# Revit family: Hager-Panelboard Meter Enclosures-Surface_mounted-IP2XC-With_Cover-Hosted-GB-en
name_source: partatom
category: Electrical Equipment
units: mm (PartAtom-declared; Revit-internal decimal feet)

## family parameters
Cut with Voids When Loaded = No
Host = Face
Maintain Annotation Orientation = Yes
Panel Configuration = Two Columns, Circuits Across
Part Type = Panelboard
Room Calculation Point = No
Round Connector Dimension = Use Diameter
Shared = No

## types (8) — shared parameters
BC_MODEL_ID = 1593630
BC_OBJECT_ID = 518755
BC_OBJECT_VERSION = #1
Classification.Uniclass.Pr.Description = Control circuit device enclosures
Classification.Uniclass.Pr.Number = Pr_80_77_28_16
Code hager = ADD-EC000214_UKME
Default Elevation = 1219 mm
EF000003 - Mounting method = Surface mounted
EF000007 - Colour = 0
EF000024 - UV resistant = No
EF000049 - Depth = 160 mm  [stored 0.524934 ft]
EF000116 - RAL-number = 7035
EF000118 - With mounting plate = No
EF001062 - EMC-version = No
EF001088 - Extension possible = No
EF001131 - Internal depth = 400 mm  [stored 1.31234 ft]
EF001134 - DIN-rail = No
EF001596 - Housing material = 0
EF004462 - Type of closure = 0
EF004464 - Type of door = Other
EF005474 - Degree of protection (IP) = IP2XC
EF006244 - Transparent cover/door = No
EF006306 - With lock = No
EF009212 - Cover model = 0
EF015777 - Neutral terminal block = No
EF015941 - Signal passing door = No
ETIM class code = EC000214
ETIM class name = Small distribution board
Ground Bus = No
HG000002-With door or cover = Yes
HG000003-Range = Panelboard Meter Enclosures
HG000005-Thickness = 3 mm  [stored 0.00984252 ft]
HG000006-Flush mounted = No
HG000018 - Cut-outs in left = No
HG000019 - Cut-outs in right = No
HG000019-Cut-outs in right = No
HG000060-RAL-number = 7035
HG000099-Onfly Template ID = 1539920
Manufacturer = Hager
Name = Panelboard Meter Enclosures-Surface_mounted-IP2XC-With_Cover-GB
Name BIM&CO = Electricity
Name hager = ADD_Enclosures_EC000214
Neutral Bus = No
Type Comments = Panelboard Meter Enclosures
Uniformat = Low Tension Service & Dist.
Uniformat code = D501001
zero-valued in all types: EF000218 - Built-in depth, EF000332 - Built-in height, EF000846 - Built-in width, EF001131 - Inner depth

## per-type parameters (varying)
| type | BC_VARIANT_ID | EF000008 - Width | EF000040 - Height | EF000266 - Number of rows | EF000339 - Type of covering | EF002950 - Width in number of modular spacings | EF015776 - Earthing terminal block | HG000001-Number of columns | HG000004-Manufacturer reference | HG000018-Cut-outs in left | HG000025-Number of cut-outs | Model |
| Panelboard Meter Enclosures-Surface_mounted_W350_H1250_D160_4_Modular_Spacing-JF12504SM | 1197421 | 350 mm  [stored 1.14829 ft] | 1250 mm  [stored 4.10105 ft] | 0 | 0 | 4 | No | 1 | JF12504SM | Yes | 4 | JF12504SM |
| Panelboard Meter Enclosures-Surface_mounted_W350_H1400_D160_6_Modular_Spacing-JF14006SM | 1197422 | 350 mm  [stored 1.14829 ft] | 1400 mm  [stored 4.59318 ft] | 0 | 0 | 6 | Yes | 1 | JF14006SM | Yes | 6 | JF14006SM |
| Panelboard Meter Enclosures-Surface_mounted_W350_H1550_D160_8_Modular_Spacing-JF15508SM | 1197423 | 350 mm  [stored 1.14829 ft] | 1550 mm  [stored 5.0853 ft] | 0 | 0 | 8 | No | 1 | JF15508SM | Yes | 8 | JF15508SM |
| Panelboard Meter Enclosures-Surface_mounted_W350_H1700_D160_9_Modular_Spacing-JF17009SM | 1197424 | 350 mm  [stored 1.14829 ft] | 1700 mm  [stored 5.57743 ft] | 0 | 0 | 9 | Yes | 1 | JF17009SM | Yes | 9 | JF17009SM |
| Panelboard Meter Enclosures-Surface_mounted_W900_H300_D160_4_Modular_Spacing-JF3004TM | 1197425 | 900 mm  [stored 2.95276 ft] | 300 mm | 1 | Door | 4 | Yes | 4 | JF3004TM | No | 4 | JF3004TM |
| Panelboard Meter Enclosures-Surface_mounted_W350_H300_D160_0_Modular_Spacing-JF300CF | 1197426 | 350 mm  [stored 1.14829 ft] | 300 mm | 0 | Door | 0 | Yes | 0 | JF300CF | No | 0 | JF300CF |
| Panelboard Meter Enclosures-Surface_mounted_W900_H450_D160_8_Modular_Spacing-JF4508TM | 1197427 | 900 mm  [stored 2.95276 ft] | 450 mm  [stored 1.47638 ft] | 2 | Door | 8 | Yes | 4 | JF4508TM | No | 8 | JF4508TM |
| Panelboard Meter Enclosures-Surface_mounted_W350_H450_D160_0_Modular_Spacing-JF450CF | 1197428 | 350 mm  [stored 1.14829 ft] | 450 mm  [stored 1.47638 ft] | 0 | Door | 0 | Yes | 0 | JF450CF | No | 0 | JF450CF |

note: column(s) folded — value = type name in every type: Reference

note: [stored X ft] marks values corroborated as IEEE doubles in the binary element streams (Revit-internal decimal feet)

## geometry (parser evidence)
native form markers: Sweep x8
no freeform markers — native parametric forms only
